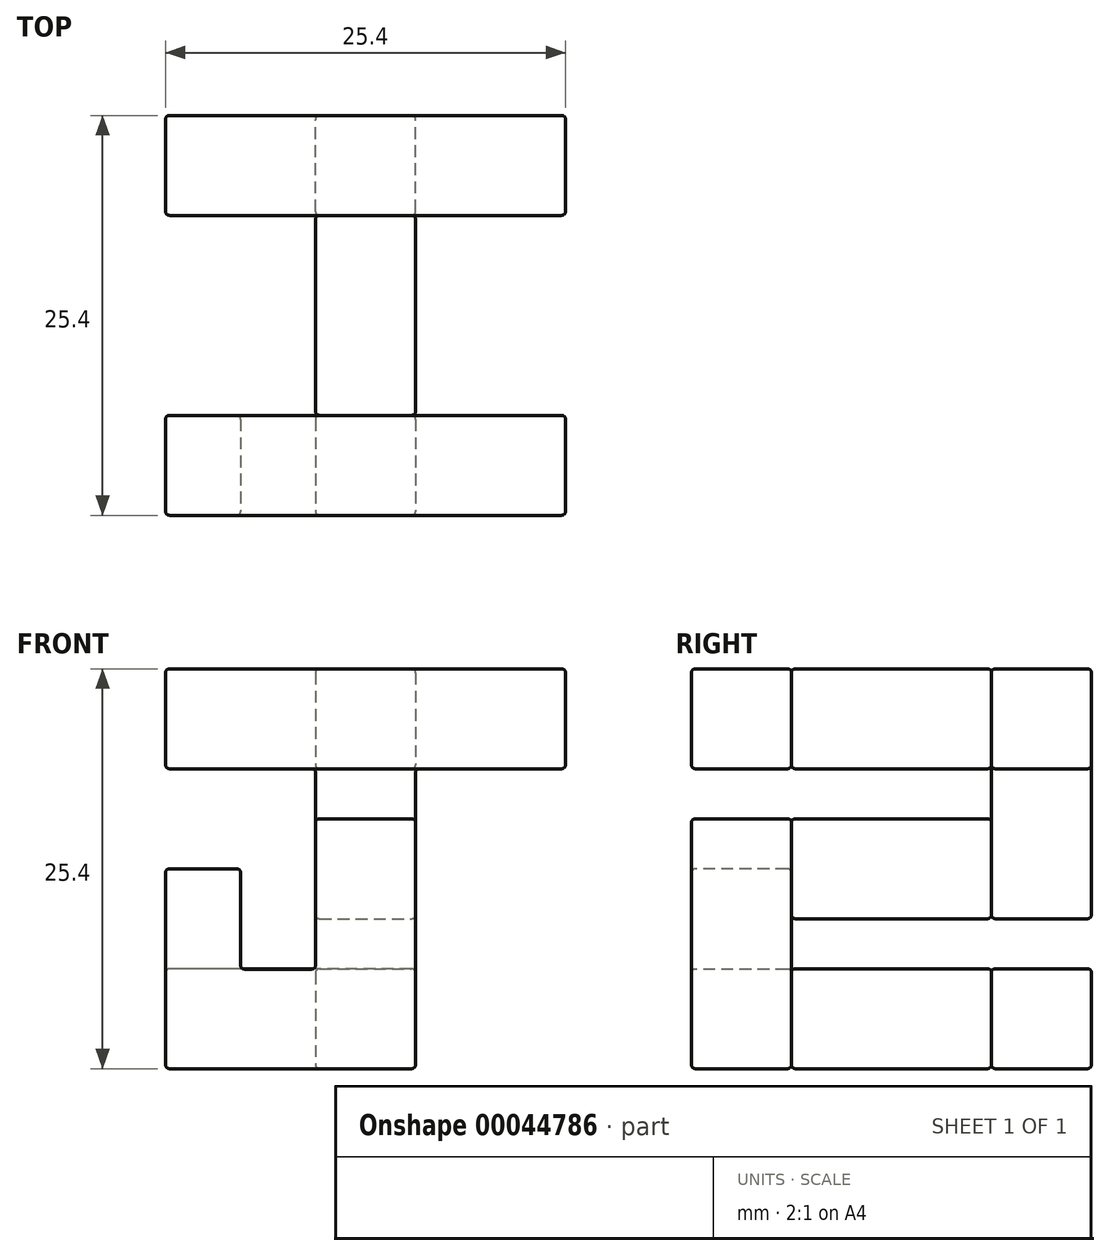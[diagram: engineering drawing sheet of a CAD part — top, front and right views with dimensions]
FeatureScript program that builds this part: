
annotation { "Feature Type Name" : "Feature", "Feature Type Description" : "" }
export const myFeature = defineFeature(function(context is Context, id is Id, definition is map)
    precondition{}
    {
        {
            var Q0;
            Q0=qCreatedBy(makeId("Front.planeOp"),FACE);
            cPlane(context, id + "F0", {"entities" : qUnion([Q0]), "cplaneType" : CPlaneType.OFFSET, "offset" : 25.4 * mm, "width" : 152.4 * mm, "height" : 152.4 * mm});
        }
        {
            var Q0;
            Q0=qCreatedBy(id+"F0.planeOp",FACE);
            var sketch = newSketch(context, id + "F1", { "sketchPlane" : qUnion([Q0])});
            skLineSegment(sketch, "E0.bottom", {"start": v(0, 0) * mm, "end": v(15.88, 0) * mm});
            skLineSegment(sketch, "E0.top", {"start": v(0, 25.4) * mm, "end": v(25.4, 25.4) * mm});
            skLineSegment(sketch, "E0.left", {"start": v(0, 0) * mm, "end": v(0, 12.7) * mm});
            skLineSegment(sketch, "E0.right", {"start": v(25.4, 19.05) * mm, "end": v(25.4, 25.4) * mm});
            skLineSegment(sketch, "E1", {"start": v(0, 25.4) * mm, "end": v(0, 19.05) * mm});
            skLineSegment(sketch, "E2", {"start": v(0, 19.05) * mm, "end": v(25.4, 19.05) * mm});
            skLineSegment(sketch, "E3", {"start": v(0, 12.7) * mm, "end": v(4.76, 12.7) * mm});
            skLineSegment(sketch, "E4", {"start": v(4.76, 12.7) * mm, "end": v(4.76, 6.32) * mm});
            skLineSegment(sketch, "E5", {"start": v(4.76, 6.32) * mm, "end": v(9.52, 6.32) * mm});
            skLineSegment(sketch, "E6", {"start": v(9.52, 6.32) * mm, "end": v(9.52, 15.88) * mm});
            skLineSegment(sketch, "E7", {"start": v(9.52, 15.88) * mm, "end": v(15.88, 15.88) * mm});
            skLineSegment(sketch, "E8", {"start": v(15.88, 15.88) * mm, "end": v(15.88, 0) * mm});
            skLineSegment(sketch, "E9", {"start": v(15.88, 0) * mm, "end": v(0, 0) * mm});
            skLineSegment(sketch, "E10.trimOffspring", {"start": v(0, 19.05) * mm, "end": v(0, 25.4) * mm});
            skSolve(sketch);
        }
        {
            var Q0;
            Q0 = qSketchRegion(id + "F1", true);
            extrude(context, id + "F2", {"entities" : qUnion([Q0]), "oppositeDirection" : true, "depth" : 6.35 * mm});
        }
        {
            var Q0;
            Q0=qCreatedBy(makeId("Front.planeOp"),FACE);
            var sketch = newSketch(context, id + "F3", { "sketchPlane" : qUnion([Q0])});
            skLineSegment(sketch, "E11.bottom", {"start": v(0, 0) * mm, "end": v(15.88, 0) * mm});
            skLineSegment(sketch, "E11.top", {"start": v(0, 25.4) * mm, "end": v(25.4, 25.4) * mm});
            skLineSegment(sketch, "E11.left", {"start": v(0, 0) * mm, "end": v(0, 6.35) * mm});
            skLineSegment(sketch, "E11.right", {"start": v(25.4, 19.05) * mm, "end": v(25.4, 25.4) * mm});
            skLineSegment(sketch, "E12", {"start": v(25.4, 25.4) * mm, "end": v(25.4, 19.05) * mm});
            skLineSegment(sketch, "E13", {"start": v(25.4, 19.05) * mm, "end": v(15.87, 19.05) * mm});
            skLineSegment(sketch, "E14", {"start": v(15.87, 19.05) * mm, "end": v(15.87, 9.52) * mm});
            skLineSegment(sketch, "E15", {"start": v(15.87, 9.52) * mm, "end": v(9.53, 9.52) * mm});
            skLineSegment(sketch, "E16", {"start": v(9.53, 9.52) * mm, "end": v(9.53, 19.05) * mm});
            skLineSegment(sketch, "E17", {"start": v(9.53, 19.05) * mm, "end": v(0, 19.05) * mm});
            skLineSegment(sketch, "E18", {"start": v(0, 19.05) * mm, "end": v(0, 25.4) * mm});
            skLineSegment(sketch, "E19", {"start": v(15.88, 0) * mm, "end": v(15.88, 6.35) * mm});
            skLineSegment(sketch, "E20", {"start": v(15.88, 6.35) * mm, "end": v(0, 6.35) * mm});
            skLineSegment(sketch, "E21", {"start": v(0, 6.35) * mm, "end": v(0, 0) * mm});
            skSolve(sketch);
        }
        {
            var Q0;
            Q0 = qSketchRegion(id + "F3", true);
            extrude(context, id + "F4", {"entities" : qUnion([Q0]), "operationType" : NewBodyOperationType.ADD, "depth" : 6.35 * mm});
        }
        {
            var Q0;
            Q0=qCreatedBy(makeId("Right.planeOp"),FACE);
            var sketch = newSketch(context, id + "F5", { "sketchPlane" : qUnion([Q0])});
            skLineSegment(sketch, "E22.bottom", {"start": v(-6.35, 0) * mm, "end": v(-19.05, 0) * mm});
            skLineSegment(sketch, "E22.top", {"start": v(-6.35, 25.4) * mm, "end": v(-19.05, 25.4) * mm});
            skLineSegment(sketch, "E23", {"start": v(-19.05, 19.05) * mm, "end": v(-6.35, 19.05) * mm});
            skLineSegment(sketch, "E24", {"start": v(-19.05, 6.35) * mm, "end": v(-6.35, 6.35) * mm});
            skLineSegment(sketch, "E25", {"start": v(-19.05, 15.88) * mm, "end": v(-6.35, 15.88) * mm});
            skLineSegment(sketch, "E26", {"start": v(-6.35, 9.53) * mm, "end": v(-19.05, 9.53) * mm});
            skLineSegment(sketch, "E27", {"start": v(-19.05, 25.4) * mm, "end": v(-19.05, 19.05) * mm});
            skLineSegment(sketch, "E28", {"start": v(-6.35, 25.4) * mm, "end": v(-6.35, 19.05) * mm});
            skLineSegment(sketch, "E29.trimOffspring", {"start": v(-19.05, 15.88) * mm, "end": v(-19.05, 9.53) * mm});
            skLineSegment(sketch, "E30.trimOffspring", {"start": v(-6.35, 15.88) * mm, "end": v(-6.35, 9.53) * mm});
            skPoint(sketch, "E31.orphan", {"position": v(-0.13, 19.05) * mm});
            skPoint(sketch, "E32.orphan", {"position": v(0, 15.88) * mm});
            skPoint(sketch, "E33.orphan", {"position": v(0, 9.53) * mm});
            skPoint(sketch, "E22.left.end.orphan", {"position": v(-0.13, 6.35) * mm});
            skLineSegment(sketch, "E34.trimOffspring", {"start": v(-19.05, 6.35) * mm, "end": v(-19.05, 0) * mm});
            skLineSegment(sketch, "E35.trimOffspring", {"start": v(-6.35, 6.35) * mm, "end": v(-6.35, 0) * mm});
            skSolve(sketch);
        }
        {
            var Q0;
            Q0 = qSketchRegion(id + "F5", true);
            extrude(context, id + "F6", {"entities" : qUnion([Q0]), "oppositeDirection" : true, "depth" : 6.35 * mm});
        }
        {
            var Q0;
            Q0=makeQuery(id+"F6.opExtrude","SWEPT_BODY",BODY,{"disambiguationData":[OSD([sQuery(id+"F5.wireOp",EDGE,"E22.bottom"),sQuery(id+"F5.wireOp",EDGE,"E24"),sQuery(id+"F5.wireOp",EDGE,"E34.trimOffspring"),sQuery(id+"F5.wireOp",EDGE,"E35.trimOffspring")])]});
            var Q1;
            Q1=makeQuery(id+"F6.opExtrude","SWEPT_BODY",BODY,{"disambiguationData":[OSD([sQuery(id+"F5.wireOp",EDGE,"E22.top"),sQuery(id+"F5.wireOp",EDGE,"E23"),sQuery(id+"F5.wireOp",EDGE,"E27"),sQuery(id+"F5.wireOp",EDGE,"E28")])]});
            var Q2;
            Q2=makeQuery(id+"F6.opExtrude","SWEPT_BODY",BODY,{"disambiguationData":[OSD([sQuery(id+"F5.wireOp",EDGE,"E25"),sQuery(id+"F5.wireOp",EDGE,"E26"),sQuery(id+"F5.wireOp",EDGE,"E29.trimOffspring"),sQuery(id+"F5.wireOp",EDGE,"E30.trimOffspring")])]});
            transform(context, id + "F7", {"entities" : qUnion([Q0, Q1, Q2]), "transformType" : TransformType.TRANSLATION_3D, "dx" : 15.88 * mm, "dy" : 0 * mm, "dz" : 0 * mm, "makeCopy" : false});
        }
        {
            var Q0;
            Q0=makeQuery(id+"F2.opExtrude","SWEPT_FACE",FACE,{"disambiguationData":[OSD([sQuery(id+"F1.wireOp",EDGE,"E0.top")])]});
            var Q1;
            Q1=makeQuery(id+"F2.opExtrude","CAP_FACE",FACE,{"disambiguationData":[OSD([sQuery(id+"F1.wireOp",EDGE,"E0.top"),sQuery(id+"F1.wireOp",EDGE,"E0.right"),sQuery(id+"F1.wireOp",EDGE,"E2"),sQuery(id+"F1.wireOp",EDGE,"E10.trimOffspring")])],"isStart":true});
            var Q2;
            Q2=makeQuery(id+"F2.opExtrude","CAP_FACE",FACE,{"disambiguationData":[OSD([sQuery(id+"F1.wireOp",EDGE,"E0.top"),sQuery(id+"F1.wireOp",EDGE,"E0.right"),sQuery(id+"F1.wireOp",EDGE,"E2"),sQuery(id+"F1.wireOp",EDGE,"E10.trimOffspring")])],"isStart":false});
            var Q3;
            Q3=makeQuery(id+"F2.opExtrude","SWEPT_FACE",FACE,{"disambiguationData":[OSD([sQuery(id+"F1.wireOp",EDGE,"E2")])]});
            var Q4;
            Q4=makeQuery(id+"F2.opExtrude","CAP_FACE",FACE,{"disambiguationData":[OSD([sQuery(id+"F1.wireOp",EDGE,"E0.left"),sQuery(id+"F1.wireOp",EDGE,"E3"),sQuery(id+"F1.wireOp",EDGE,"E4"),sQuery(id+"F1.wireOp",EDGE,"E5"),sQuery(id+"F1.wireOp",EDGE,"E6"),sQuery(id+"F1.wireOp",EDGE,"E7"),sQuery(id+"F1.wireOp",EDGE,"E8"),sQuery(id+"F1.wireOp",EDGE,"E9")])],"isStart":false});
            var Q5;
            Q5=makeQuery(id+"F2.opExtrude","CAP_FACE",FACE,{"disambiguationData":[OSD([sQuery(id+"F1.wireOp",EDGE,"E0.left"),sQuery(id+"F1.wireOp",EDGE,"E3"),sQuery(id+"F1.wireOp",EDGE,"E4"),sQuery(id+"F1.wireOp",EDGE,"E5"),sQuery(id+"F1.wireOp",EDGE,"E6"),sQuery(id+"F1.wireOp",EDGE,"E7"),sQuery(id+"F1.wireOp",EDGE,"E8"),sQuery(id+"F1.wireOp",EDGE,"E9")])],"isStart":true});
            var Q6;
            Q6=makeQuery(id+"F2.opExtrude","SWEPT_EDGE",EDGE,{"disambiguationData":[OSD([sQuery(id+"F1.wireOp",EDGE,"E0.left"),sQuery(id+"F1.wireOp",EDGE,"E9")])]});
            var Q7;
            Q7=makeQuery(id+"F2.opExtrude","SWEPT_EDGE",EDGE,{"disambiguationData":[OSD([sQuery(id+"F1.wireOp",EDGE,"E0.left"),sQuery(id+"F1.wireOp",EDGE,"E3")])]});
            var Q8;
            Q8=makeQuery(id+"F2.opExtrude","SWEPT_EDGE",EDGE,{"disambiguationData":[OSD([sQuery(id+"F1.wireOp",EDGE,"E3"),sQuery(id+"F1.wireOp",EDGE,"E4")])]});
            var Q9;
            Q9=makeQuery(id+"F2.opExtrude","SWEPT_EDGE",EDGE,{"disambiguationData":[OSD([sQuery(id+"F1.wireOp",EDGE,"E4"),sQuery(id+"F1.wireOp",EDGE,"E5")])]});
            var Q10;
            Q10=makeQuery(id+"F2.opExtrude","SWEPT_EDGE",EDGE,{"disambiguationData":[OSD([sQuery(id+"F1.wireOp",EDGE,"E7"),sQuery(id+"F1.wireOp",EDGE,"E8")])]});
            var Q11;
            Q11=makeQuery(id+"F2.opExtrude","SWEPT_EDGE",EDGE,{"disambiguationData":[OSD([sQuery(id+"F1.wireOp",EDGE,"E6"),sQuery(id+"F1.wireOp",EDGE,"E7")])]});
            var Q12;
            Q12=makeQuery(id+"F2.opExtrude","SWEPT_EDGE",EDGE,{"disambiguationData":[OSD([sQuery(id+"F1.wireOp",EDGE,"E5"),sQuery(id+"F1.wireOp",EDGE,"E6")])]});
            var Q13;
            Q13=makeQuery(id+"F2.opExtrude","SWEPT_EDGE",EDGE,{"disambiguationData":[OSD([sQuery(id+"F1.wireOp",EDGE,"E8"),sQuery(id+"F1.wireOp",EDGE,"E9")])]});
            var Q14;
            Q14=makeQuery(id+"F4.opExtrude","CAP_FACE",FACE,{"disambiguationData":[OSD([sQuery(id+"F3.wireOp",EDGE,"E11.top"),sQuery(id+"F3.wireOp",EDGE,"E12"),sQuery(id+"F3.wireOp",EDGE,"E13"),sQuery(id+"F3.wireOp",EDGE,"E14"),sQuery(id+"F3.wireOp",EDGE,"E15"),sQuery(id+"F3.wireOp",EDGE,"E16"),sQuery(id+"F3.wireOp",EDGE,"E17"),sQuery(id+"F3.wireOp",EDGE,"E18")])],"isStart":false});
            var Q15;
            Q15=makeQuery(id+"F4.opExtrude","SWEPT_FACE",FACE,{"disambiguationData":[OSD([sQuery(id+"F3.wireOp",EDGE,"E11.top")])]});
            var Q16;
            Q16=makeQuery(id+"F4.opExtrude","CAP_FACE",FACE,{"disambiguationData":[OSD([sQuery(id+"F3.wireOp",EDGE,"E11.top"),sQuery(id+"F3.wireOp",EDGE,"E12"),sQuery(id+"F3.wireOp",EDGE,"E13"),sQuery(id+"F3.wireOp",EDGE,"E14"),sQuery(id+"F3.wireOp",EDGE,"E15"),sQuery(id+"F3.wireOp",EDGE,"E16"),sQuery(id+"F3.wireOp",EDGE,"E17"),sQuery(id+"F3.wireOp",EDGE,"E18")])],"isStart":true});
            var Q17;
            Q17=makeQuery(id+"F4.opExtrude","SWEPT_FACE",FACE,{"disambiguationData":[OSD([sQuery(id+"F3.wireOp",EDGE,"E16")])]});
            var Q18;
            Q18=makeQuery(id+"F4.opExtrude","SWEPT_FACE",FACE,{"disambiguationData":[OSD([sQuery(id+"F3.wireOp",EDGE,"E17")])]});
            var Q19;
            Q19=makeQuery(id+"F4.opExtrude","SWEPT_FACE",FACE,{"disambiguationData":[OSD([sQuery(id+"F3.wireOp",EDGE,"E18")])]});
            var Q20;
            Q20=makeQuery(id+"F4.opExtrude","SWEPT_FACE",FACE,{"disambiguationData":[OSD([sQuery(id+"F3.wireOp",EDGE,"E14")])]});
            var Q21;
            Q21=makeQuery(id+"F4.opExtrude","SWEPT_FACE",FACE,{"disambiguationData":[OSD([sQuery(id+"F3.wireOp",EDGE,"E15")])]});
            var Q22;
            Q22=makeQuery(id+"F4.opExtrude","SWEPT_FACE",FACE,{"disambiguationData":[OSD([sQuery(id+"F3.wireOp",EDGE,"E13")])]});
            var Q23;
            Q23=makeQuery(id+"F4.opExtrude","CAP_FACE",FACE,{"disambiguationData":[OSD([sQuery(id+"F3.wireOp",EDGE,"E11.bottom"),sQuery(id+"F3.wireOp",EDGE,"E19"),sQuery(id+"F3.wireOp",EDGE,"E20"),sQuery(id+"F3.wireOp",EDGE,"E21")])],"isStart":true});
            var Q24;
            Q24=makeQuery(id+"F4.opExtrude","SWEPT_FACE",FACE,{"disambiguationData":[OSD([sQuery(id+"F3.wireOp",EDGE,"E20")])]});
            var Q25;
            Q25=makeQuery(id+"F4.opExtrude","SWEPT_FACE",FACE,{"disambiguationData":[OSD([sQuery(id+"F3.wireOp",EDGE,"E11.bottom")])]});
            var Q26;
            Q26=makeQuery(id+"F4.opExtrude","CAP_FACE",FACE,{"disambiguationData":[OSD([sQuery(id+"F3.wireOp",EDGE,"E11.bottom"),sQuery(id+"F3.wireOp",EDGE,"E19"),sQuery(id+"F3.wireOp",EDGE,"E20"),sQuery(id+"F3.wireOp",EDGE,"E21")])],"isStart":false});
            var Q27;
            Q27=makeQuery(id+"F6.opExtrude","SWEPT_FACE",FACE,{"disambiguationData":[OSD([sQuery(id+"F5.wireOp",EDGE,"E34.trimOffspring")])]});
            var Q28;
            Q28=makeQuery(id+"F6.opExtrude","CAP_EDGE",EDGE,{"disambiguationData":[OSD([sQuery(id+"F5.wireOp",EDGE,"E22.bottom")])],"isStart":false});
            var Q29;
            Q29=makeQuery(id+"F6.opExtrude","CAP_EDGE",EDGE,{"disambiguationData":[OSD([sQuery(id+"F5.wireOp",EDGE,"E24")])],"isStart":false});
            var Q30;
            Q30=makeQuery(id+"F6.opExtrude","CAP_EDGE",EDGE,{"disambiguationData":[OSD([sQuery(id+"F5.wireOp",EDGE,"E22.bottom")])],"isStart":true});
            var Q31;
            Q31=makeQuery(id+"F6.opExtrude","CAP_EDGE",EDGE,{"disambiguationData":[OSD([sQuery(id+"F5.wireOp",EDGE,"E24")])],"isStart":true});
            var Q32;
            Q32=makeQuery(id+"F6.opExtrude","SWEPT_FACE",FACE,{"disambiguationData":[OSD([sQuery(id+"F5.wireOp",EDGE,"E35.trimOffspring")])]});
            var Q33;
            Q33=makeQuery(id+"F6.opExtrude","CAP_FACE",FACE,{"disambiguationData":[OSD([sQuery(id+"F5.wireOp",EDGE,"E22.top"),sQuery(id+"F5.wireOp",EDGE,"E23"),sQuery(id+"F5.wireOp",EDGE,"E27"),sQuery(id+"F5.wireOp",EDGE,"E28")])],"isStart":true});
            var Q34;
            Q34=makeQuery(id+"F6.opExtrude","SWEPT_FACE",FACE,{"disambiguationData":[OSD([sQuery(id+"F5.wireOp",EDGE,"E23")])]});
            var Q35;
            Q35=makeQuery(id+"F6.opExtrude","CAP_FACE",FACE,{"disambiguationData":[OSD([sQuery(id+"F5.wireOp",EDGE,"E22.top"),sQuery(id+"F5.wireOp",EDGE,"E23"),sQuery(id+"F5.wireOp",EDGE,"E27"),sQuery(id+"F5.wireOp",EDGE,"E28")])],"isStart":false});
            var Q36;
            Q36=makeQuery(id+"F6.opExtrude","SWEPT_FACE",FACE,{"disambiguationData":[OSD([sQuery(id+"F5.wireOp",EDGE,"E22.top")])]});
            var Q37;
            Q37=makeQuery(id+"F6.opExtrude","SWEPT_FACE",FACE,{"disambiguationData":[OSD([sQuery(id+"F5.wireOp",EDGE,"E25")])]});
            var Q38;
            Q38=makeQuery(id+"F6.opExtrude","CAP_FACE",FACE,{"disambiguationData":[OSD([sQuery(id+"F5.wireOp",EDGE,"E25"),sQuery(id+"F5.wireOp",EDGE,"E26"),sQuery(id+"F5.wireOp",EDGE,"E29.trimOffspring"),sQuery(id+"F5.wireOp",EDGE,"E30.trimOffspring")])],"isStart":true});
            var Q39;
            Q39=makeQuery(id+"F6.opExtrude","SWEPT_FACE",FACE,{"disambiguationData":[OSD([sQuery(id+"F5.wireOp",EDGE,"E26")])]});
            var Q40;
            Q40=makeQuery(id+"F6.opExtrude","CAP_FACE",FACE,{"disambiguationData":[OSD([sQuery(id+"F5.wireOp",EDGE,"E25"),sQuery(id+"F5.wireOp",EDGE,"E26"),sQuery(id+"F5.wireOp",EDGE,"E29.trimOffspring"),sQuery(id+"F5.wireOp",EDGE,"E30.trimOffspring")])],"isStart":false});
            fillet(context, id + "F8", {"entities" : qUnion([Q0, Q1, Q2, Q3, Q4, Q5, Q6, Q7, Q8, Q9, Q10, Q11, Q12, Q13, Q14, Q15, Q16, Q17, Q18, Q19, Q20, Q21, Q22, Q23, Q24, Q25, Q26, Q27, Q28, Q29, Q30, Q31, Q32, Q33, Q34, Q35, Q36, Q37, Q38, Q39, Q40]), "radius" : 0.25 * mm, "tangentPropagation" : true, "allowEdgeOverflow" : false});
        }
    });
